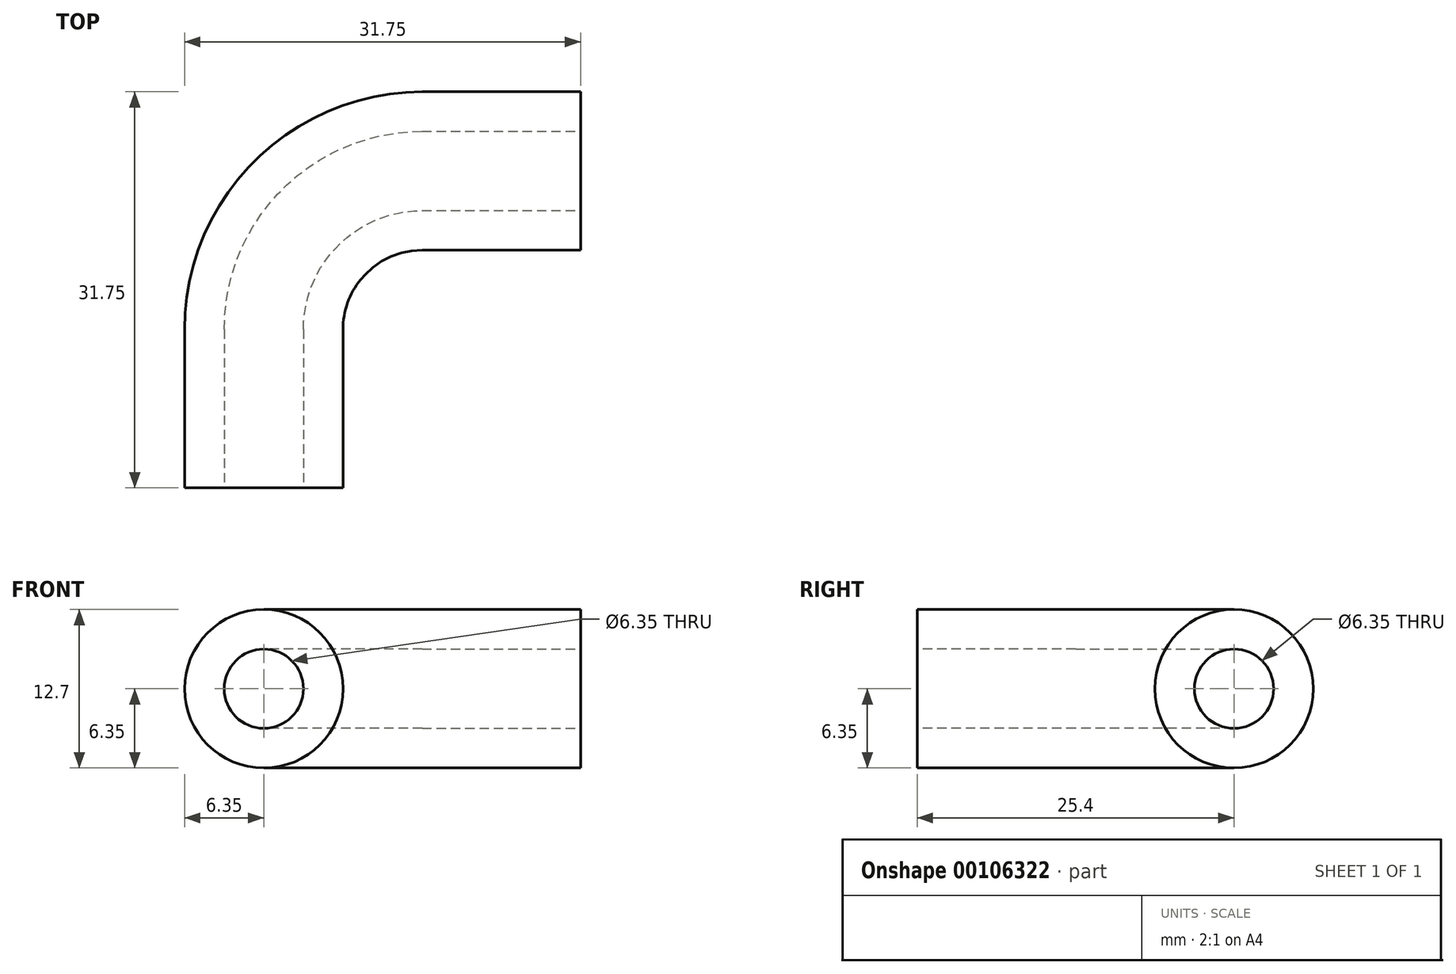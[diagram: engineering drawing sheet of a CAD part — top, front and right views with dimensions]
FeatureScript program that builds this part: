
annotation { "Feature Type Name" : "Feature", "Feature Type Description" : "" }
export const myFeature = defineFeature(function(context is Context, id is Id, definition is map)
    precondition{}
    {
        {
            var Q0;
            Q0=qCreatedBy(makeId("Right.planeOp"),FACE);
            var sketch = newSketch(context, id + "F0", { "sketchPlane" : qUnion([Q0])});
            skCircle(sketch, "E0", {"center": v(25.4, 0) * mm, "radius": 6.35 * mm});
            skCircle(sketch, "E1", {"center": v(25.4, 0) * mm, "radius": 3.18 * mm});
            skSolve(sketch);
        }
        {
            var Q0;
            Q0 = qSketchRegion(id + "F0", true);
            extrude(context, id + "F1", {"entities" : qUnion([Q0]), "oppositeDirection" : true, "depth" : 12.7 * mm});
        }
        {
            var Q0;
            Q0=qCreatedBy(makeId("Front.planeOp"),FACE);
            var sketch = newSketch(context, id + "F2", { "sketchPlane" : qUnion([Q0])});
            skCircle(sketch, "E2", {"center": v(-25.4, 0) * mm, "radius": 6.35 * mm});
            skCircle(sketch, "E3", {"center": v(-25.4, 0) * mm, "radius": 3.18 * mm});
            skSolve(sketch);
        }
        {
            var Q0;
            Q0 = qSketchRegion(id + "F2", true);
            extrude(context, id + "F3", {"entities" : qUnion([Q0]), "oppositeDirection" : true, "depth" : 12.7 * mm});
        }
        {
            var Q0;
            Q0=qCreatedBy(makeId("Top.planeOp"),FACE);
            var sketch = newSketch(context, id + "F4", { "sketchPlane" : qUnion([Q0])});
            skLineSegment(sketch, "E4", {"start": v(-12.7, 70.94) * mm, "end": v(-12.7, -7.52) * mm, "construction": true});
            skLineSegment(sketch, "E5", {"start": v(-65.35, 12.7) * mm, "end": v(-3.2, 12.7) * mm, "construction": true});
            skArc(sketch, "E6", {"start": v(-12.7, 38.1) * mm, "mid": v(-30.66, 30.66) * mm, "end": v(-38.1, 12.7) * mm});
            skSolve(sketch);
        }
        {
            var Q0;
            Q0=makeQuery(id+"F1.opExtrude","CAP_FACE",FACE,{"disambiguationData":[OSD([sQuery(id+"F0.wireOp",EDGE,"E0"),sQuery(id+"F0.wireOp",EDGE,"E1")])],"isStart":false});
            var Q1;
            Q1=sQuery(id+"F4.wireOp",EDGE,"E6");
            sweep(context, id + "F5", {"operationType" : NewBodyOperationType.ADD, "profiles" : qUnion([Q0]), "path" : qUnion([Q1])});
        }
    });
